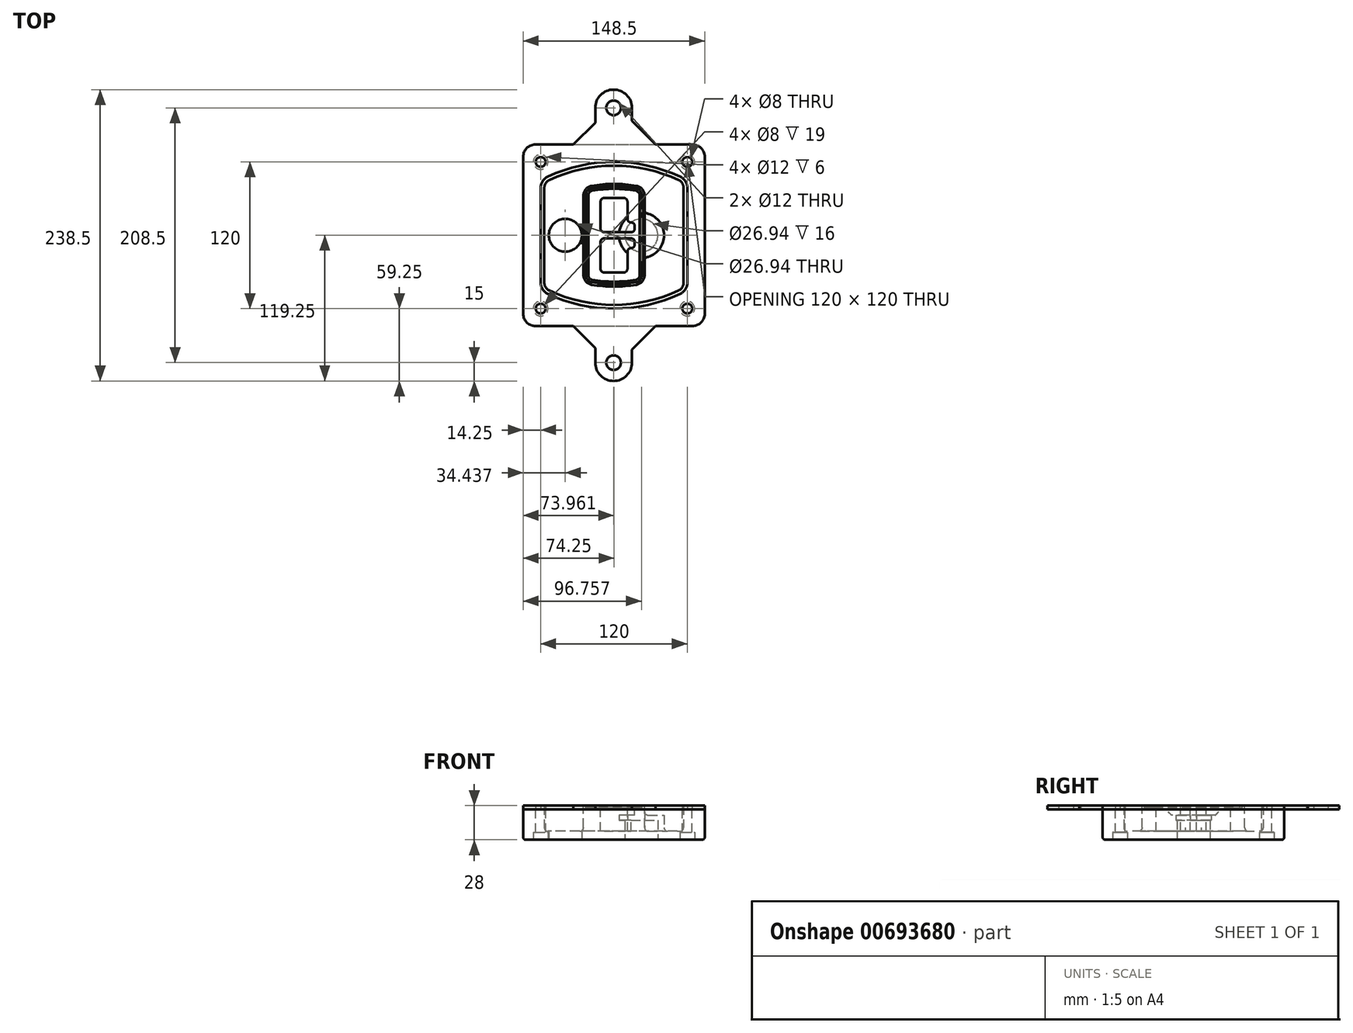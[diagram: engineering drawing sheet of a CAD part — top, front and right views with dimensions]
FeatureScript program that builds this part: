
annotation { "Feature Type Name" : "Feature", "Feature Type Description" : "" }
export const myFeature = defineFeature(function(context is Context, id is Id, definition is map)
    precondition{}
    {
        {
            var Q0;
            Q0=qCreatedBy(makeId("Top.planeOp"),FACE);
            var sketch = newSketch(context, id + "F0", { "sketchPlane" : qUnion([Q0])});
            skPoint(sketch, "E0.rect.middle", {"position": v(0, 0) * mm});
            skLineSegment(sketch, "E1.bottom", {"start": v(-64.25, -74.25) * mm, "end": v(64.25, -74.25) * mm});
            skLineSegment(sketch, "E1.top", {"start": v(-64.25, 74.25) * mm, "end": v(64.25, 74.25) * mm});
            skLineSegment(sketch, "E1.left", {"start": v(-74.25, -64.25) * mm, "end": v(-74.25, 64.25) * mm});
            skLineSegment(sketch, "E1.right", {"start": v(74.25, -64.25) * mm, "end": v(74.25, 64.25) * mm});
            skLineSegment(sketch, "E2", {"start": v(-74.25, 74.25) * mm, "end": v(74.25, -74.25) * mm, "construction": true});
            skLineSegment(sketch, "E3", {"start": v(74.25, 74.25) * mm, "end": v(-74.25, -74.25) * mm, "construction": true});
            skCircle(sketch, "E4", {"center": v(-60, 60) * mm, "radius": 4 * mm});
            skCircle(sketch, "E5", {"center": v(60, 60) * mm, "radius": 4 * mm});
            skCircle(sketch, "E6", {"center": v(60, -60) * mm, "radius": 4 * mm});
            skCircle(sketch, "E7", {"center": v(-60, -60) * mm, "radius": 4 * mm});
            skLineSegment(sketch, "E8", {"start": v(-60, 60) * mm, "end": v(60, 60) * mm, "construction": true});
            skLineSegment(sketch, "E9", {"start": v(60, 60) * mm, "end": v(60, -60) * mm, "construction": true});
            skLineSegment(sketch, "E10", {"start": v(60, -60) * mm, "end": v(-60, -60) * mm, "construction": true});
            skLineSegment(sketch, "E11", {"start": v(-60, -60) * mm, "end": v(-60, 60) * mm, "construction": true});
            skLineSegment(sketch, "E12", {"start": v(-60, 38.83) * mm, "end": v(-60, -38.83) * mm});
            skLineSegment(sketch, "E13", {"start": v(60, 38.83) * mm, "end": v(60, -38.83) * mm});
            skArc(sketch, "E14", {"start": v(54.26, 47.88) * mm, "mid": v(0, 60) * mm, "end": v(-54.26, 47.88) * mm});
            skArc(sketch, "E15", {"start": v(-54.26, -47.88) * mm, "mid": v(0, -60) * mm, "end": v(54.26, -47.88) * mm});
            skLineSegment(sketch, "E16", {"start": v(-60, 0) * mm, "end": v(60, 0) * mm, "construction": true});
            skPoint(sketch, "E17.visualSharp", {"position": v(-60, -45) * mm});
            skArc(sketch, "E17.filletArc", {"start": v(-60, -38.83) * mm, "mid": v(-58.44, -44.2) * mm, "end": v(-54.26, -47.88) * mm});
            skPoint(sketch, "E18.visualSharp", {"position": v(-60, 45) * mm});
            skArc(sketch, "E18.filletArc", {"start": v(-54.26, 47.88) * mm, "mid": v(-58.44, 44.2) * mm, "end": v(-60, 38.83) * mm});
            skPoint(sketch, "E19.visualSharp", {"position": v(60, 45) * mm});
            skArc(sketch, "E19.filletArc", {"start": v(60, 38.83) * mm, "mid": v(58.44, 44.2) * mm, "end": v(54.26, 47.88) * mm});
            skPoint(sketch, "E20.visualSharp", {"position": v(60, -45) * mm});
            skArc(sketch, "E20.filletArc", {"start": v(54.26, -47.88) * mm, "mid": v(58.44, -44.2) * mm, "end": v(60, -38.83) * mm});
            skPoint(sketch, "E21.visualSharp", {"position": v(-74.25, 74.25) * mm});
            skArc(sketch, "E21.filletArc", {"start": v(-64.25, 74.25) * mm, "mid": v(-71.32, 71.32) * mm, "end": v(-74.25, 64.25) * mm});
            skPoint(sketch, "E22.visualSharp", {"position": v(74.25, 74.25) * mm});
            skArc(sketch, "E22.filletArc", {"start": v(74.25, 64.25) * mm, "mid": v(71.32, 71.32) * mm, "end": v(64.25, 74.25) * mm});
            skPoint(sketch, "E23.visualSharp", {"position": v(74.25, -74.25) * mm});
            skArc(sketch, "E23.filletArc", {"start": v(64.25, -74.25) * mm, "mid": v(71.32, -71.32) * mm, "end": v(74.25, -64.25) * mm});
            skPoint(sketch, "E24.visualSharp", {"position": v(-74.25, -74.25) * mm});
            skArc(sketch, "E24.filletArc", {"start": v(-74.25, -64.25) * mm, "mid": v(-71.32, -71.32) * mm, "end": v(-64.25, -74.25) * mm});
            skArc(sketch, "E25.0", {"start": v(57, 38.83) * mm, "mid": v(55.9, 42.58) * mm, "end": v(52.98, 45.17) * mm});
            skLineSegment(sketch, "E25.1", {"start": v(57, 38.83) * mm, "end": v(57, -38.83) * mm});
            skArc(sketch, "E25.2", {"start": v(52.98, -45.17) * mm, "mid": v(55.9, -42.58) * mm, "end": v(57, -38.83) * mm});
            skArc(sketch, "E25.3", {"start": v(-52.98, -45.17) * mm, "mid": v(0, -57) * mm, "end": v(52.98, -45.17) * mm});
            skArc(sketch, "E25.4", {"start": v(-57, -38.83) * mm, "mid": v(-55.9, -42.58) * mm, "end": v(-52.98, -45.17) * mm});
            skArc(sketch, "E25.5", {"start": v(52.98, 45.17) * mm, "mid": v(0, 57) * mm, "end": v(-52.98, 45.17) * mm});
            skLineSegment(sketch, "E25.6", {"start": v(-57, 38.83) * mm, "end": v(-57, -38.83) * mm});
            skArc(sketch, "E25.7", {"start": v(-52.98, 45.17) * mm, "mid": v(-55.9, 42.58) * mm, "end": v(-57, 38.83) * mm});
            skArc(sketch, "E26.0", {"start": v(-55.96, 51.5) * mm, "mid": v(-61.82, 46.33) * mm, "end": v(-64, 38.83) * mm});
            skArc(sketch, "E26.1", {"start": v(55.96, 51.5) * mm, "mid": v(0, 64) * mm, "end": v(-55.96, 51.5) * mm});
            skArc(sketch, "E26.2", {"start": v(64, 38.83) * mm, "mid": v(61.82, 46.33) * mm, "end": v(55.96, 51.5) * mm});
            skLineSegment(sketch, "E26.3", {"start": v(64, 38.83) * mm, "end": v(64, -38.83) * mm});
            skArc(sketch, "E26.4", {"start": v(55.96, -51.5) * mm, "mid": v(61.82, -46.33) * mm, "end": v(64, -38.83) * mm});
            skLineSegment(sketch, "E26.5", {"start": v(-64, 38.83) * mm, "end": v(-64, -38.83) * mm});
            skArc(sketch, "E26.6", {"start": v(-55.96, -51.5) * mm, "mid": v(0, -64) * mm, "end": v(55.96, -51.5) * mm});
            skArc(sketch, "E26.7", {"start": v(-64, -38.83) * mm, "mid": v(-61.82, -46.33) * mm, "end": v(-55.96, -51.5) * mm});
            skSolve(sketch);
        }
        {
            var Q0;
            Q0=makeQuery(id+"F0.imprint","IMPRINT",FACE,{"disambiguationData":[TD([[makeQuery(id+"F0.imprint","IMPRINT",EDGE,{"derivedFrom":sQuery(id+"F0.wireOp",EDGE,"E1.bottom")}),1.0]])]});
            var Q1;
            Q1=makeQuery(id+"F0.imprint","IMPRINT",FACE,{"disambiguationData":[TD([[makeQuery(id+"F0.imprint","IMPRINT",EDGE,{"derivedFrom":sQuery(id+"F0.wireOp",EDGE,"E12")}),1.0]])]});
            var Q2;
            Q2=makeQuery(id+"F0.imprint","IMPRINT",FACE,{"disambiguationData":[TD([[makeQuery(id+"F0.imprint","IMPRINT",EDGE,{"derivedFrom":sQuery(id+"F0.wireOp",EDGE,"E25.0")}),1.0]])]});
            var Q3;
            Q3=makeQuery(id+"F0.imprint","IMPRINT",FACE,{"disambiguationData":[TD([[makeQuery(id+"F0.imprint","IMPRINT",EDGE,{"derivedFrom":sQuery(id+"F0.wireOp",EDGE,"E12")}),-1.0]])]});
            extrude(context, id + "F1", {"entities" : qUnion([Q0, Q1, Q2, Q3]), "oppositeDirection" : true, "depth" : 25 * mm});
        }
        {
            var Q0;
            Q0=makeQuery(id+"F0.imprint","IMPRINT",FACE,{"disambiguationData":[TD([[makeQuery(id+"F0.imprint","IMPRINT",EDGE,{"derivedFrom":sQuery(id+"F0.wireOp",EDGE,"E12")}),1.0]])]});
            extrude(context, id + "F2", {"entities" : qUnion([Q0]), "operationType" : NewBodyOperationType.ADD, "depth" : 3 * mm});
        }
        {
            var Q0;
            Q0=makeQuery(id+"F0.imprint","IMPRINT",FACE,{"disambiguationData":[TD([[makeQuery(id+"F0.imprint","IMPRINT",EDGE,{"derivedFrom":sQuery(id+"F0.wireOp",EDGE,"E25.0")}),1.0]])]});
            extrude(context, id + "F3", {"entities" : qUnion([Q0]), "operationType" : NewBodyOperationType.REMOVE, "oppositeDirection" : true, "depth" : 18 * mm});
        }
        {
            var Q0;
            Q0=makeQuery(id+"F2.opExtrude","CAP_FACE",FACE,{"disambiguationData":[OSD([sQuery(id+"F0.wireOp",EDGE,"E12"),sQuery(id+"F0.wireOp",EDGE,"E13"),sQuery(id+"F0.wireOp",EDGE,"E14"),sQuery(id+"F0.wireOp",EDGE,"E15"),sQuery(id+"F0.wireOp",EDGE,"E17.filletArc"),sQuery(id+"F0.wireOp",EDGE,"E18.filletArc"),sQuery(id+"F0.wireOp",EDGE,"E19.filletArc"),sQuery(id+"F0.wireOp",EDGE,"E20.filletArc"),sQuery(id+"F0.wireOp",EDGE,"E25.0"),sQuery(id+"F0.wireOp",EDGE,"E25.1"),sQuery(id+"F0.wireOp",EDGE,"E25.2"),sQuery(id+"F0.wireOp",EDGE,"E25.3"),sQuery(id+"F0.wireOp",EDGE,"E25.4"),sQuery(id+"F0.wireOp",EDGE,"E25.5"),sQuery(id+"F0.wireOp",EDGE,"E25.6"),sQuery(id+"F0.wireOp",EDGE,"E25.7")])],"isStart":false});
            var sketch = newSketch(context, id + "F4", { "sketchPlane" : qUnion([Q0])});
            skArc(sketch, "E27.0", {"start": v(-18.34, -40.45) * mm, "mid": v(0, -42) * mm, "end": v(18.34, -40.45) * mm});
            skArc(sketch, "E28.0", {"start": v(18.34, 40.45) * mm, "mid": v(0, 42) * mm, "end": v(-18.34, 40.45) * mm});
            skLineSegment(sketch, "E29", {"start": v(-25, 32.57) * mm, "end": v(-25, -32.57) * mm});
            skLineSegment(sketch, "E30", {"start": v(25, 32.57) * mm, "end": v(25, -32.57) * mm});
            skLineSegment(sketch, "E31", {"start": v(-25, 39.1) * mm, "end": v(25, 39.1) * mm, "construction": true});
            skLineSegment(sketch, "E32", {"start": v(-25, -39.1) * mm, "end": v(25, -39.1) * mm, "construction": true});
            skPoint(sketch, "E33.visualSharp", {"position": v(-25, 39.1) * mm});
            skArc(sketch, "E33.filletArc", {"start": v(-18.34, 40.45) * mm, "mid": v(-23.11, 37.73) * mm, "end": v(-25, 32.57) * mm});
            skPoint(sketch, "E34.visualSharp", {"position": v(25, 39.1) * mm});
            skArc(sketch, "E34.filletArc", {"start": v(25, 32.57) * mm, "mid": v(23.11, 37.73) * mm, "end": v(18.34, 40.45) * mm});
            skPoint(sketch, "E35.visualSharp", {"position": v(25, -39.1) * mm});
            skArc(sketch, "E35.filletArc", {"start": v(18.34, -40.45) * mm, "mid": v(23.11, -37.73) * mm, "end": v(25, -32.57) * mm});
            skPoint(sketch, "E36.visualSharp", {"position": v(-25, -39.1) * mm});
            skArc(sketch, "E36.filletArc", {"start": v(-25, -32.57) * mm, "mid": v(-23.11, -37.73) * mm, "end": v(-18.34, -40.45) * mm});
            skArc(sketch, "E37.0", {"start": v(52.98, 45.17) * mm, "mid": v(0, 57) * mm, "end": v(-52.98, 45.17) * mm});
            skArc(sketch, "E37.1", {"start": v(-52.98, 45.17) * mm, "mid": v(-55.9, 42.58) * mm, "end": v(-57, 38.83) * mm});
            skLineSegment(sketch, "E37.2", {"start": v(-57, 38.83) * mm, "end": v(-57, -38.83) * mm});
            skArc(sketch, "E37.3", {"start": v(-57, -38.83) * mm, "mid": v(-55.9, -42.58) * mm, "end": v(-52.98, -45.17) * mm});
            skArc(sketch, "E37.4", {"start": v(-52.98, -45.17) * mm, "mid": v(0, -57) * mm, "end": v(52.98, -45.17) * mm});
            skArc(sketch, "E37.5", {"start": v(52.98, -45.17) * mm, "mid": v(55.9, -42.58) * mm, "end": v(57, -38.83) * mm});
            skLineSegment(sketch, "E37.6", {"start": v(57, 38.83) * mm, "end": v(57, -38.83) * mm});
            skArc(sketch, "E37.7", {"start": v(57, 38.83) * mm, "mid": v(55.9, 42.58) * mm, "end": v(52.98, 45.17) * mm});
            skLineSegment(sketch, "E38.0", {"start": v(23, 32.57) * mm, "end": v(23, -32.57) * mm});
            skArc(sketch, "E38.1", {"start": v(18, -38.48) * mm, "mid": v(21.58, -36.44) * mm, "end": v(23, -32.57) * mm});
            skArc(sketch, "E38.2", {"start": v(-18, -38.48) * mm, "mid": v(0, -40) * mm, "end": v(18, -38.48) * mm});
            skArc(sketch, "E38.3", {"start": v(-23, -32.57) * mm, "mid": v(-21.58, -36.44) * mm, "end": v(-18, -38.48) * mm});
            skLineSegment(sketch, "E38.4", {"start": v(-23, 32.57) * mm, "end": v(-23, -32.57) * mm});
            skArc(sketch, "E38.5", {"start": v(23, 32.57) * mm, "mid": v(21.58, 36.44) * mm, "end": v(18, 38.48) * mm});
            skArc(sketch, "E38.6", {"start": v(-18, 38.48) * mm, "mid": v(-21.58, 36.44) * mm, "end": v(-23, 32.57) * mm});
            skArc(sketch, "E38.7", {"start": v(18, 38.48) * mm, "mid": v(0, 40) * mm, "end": v(-18, 38.48) * mm});
            skArc(sketch, "E39.0", {"start": v(21, 32.57) * mm, "mid": v(20.06, 35.15) * mm, "end": v(17.67, 36.5) * mm});
            skLineSegment(sketch, "E39.1", {"start": v(21, 32.57) * mm, "end": v(21, -32.57) * mm});
            skArc(sketch, "E39.2", {"start": v(17.67, -36.5) * mm, "mid": v(20.06, -35.15) * mm, "end": v(21, -32.57) * mm});
            skArc(sketch, "E39.3", {"start": v(-17.67, -36.5) * mm, "mid": v(0, -38) * mm, "end": v(17.67, -36.5) * mm});
            skArc(sketch, "E39.4", {"start": v(-21, -32.57) * mm, "mid": v(-20.06, -35.15) * mm, "end": v(-17.67, -36.5) * mm});
            skArc(sketch, "E39.5", {"start": v(17.67, 36.5) * mm, "mid": v(0, 38) * mm, "end": v(-17.67, 36.5) * mm});
            skLineSegment(sketch, "E39.6", {"start": v(-21, 32.57) * mm, "end": v(-21, -32.57) * mm});
            skArc(sketch, "E39.7", {"start": v(-17.67, 36.5) * mm, "mid": v(-20.06, 35.15) * mm, "end": v(-21, 32.57) * mm});
            skLineSegment(sketch, "E40", {"start": v(-25, 0) * mm, "end": v(25, 0) * mm, "construction": true});
            skLineSegment(sketch, "E41", {"start": v(-11, 5.5) * mm, "end": v(-11, 27.5) * mm});
            skLineSegment(sketch, "E42", {"start": v(-8, 30.5) * mm, "end": v(8, 30.5) * mm});
            skLineSegment(sketch, "E43", {"start": v(11, 27.5) * mm, "end": v(11, 13.5) * mm});
            skLineSegment(sketch, "E44", {"start": v(14, 10.5) * mm, "end": v(14, 10.5) * mm});
            skLineSegment(sketch, "E45", {"start": v(17, 7.5) * mm, "end": v(17, 5.5) * mm});
            skLineSegment(sketch, "E46", {"start": v(14, 2.5) * mm, "end": v(-8, 2.5) * mm});
            skPoint(sketch, "E47.visualSharp", {"position": v(-11, 30.5) * mm});
            skArc(sketch, "E47.filletArc", {"start": v(-8, 30.5) * mm, "mid": v(-10.12, 29.62) * mm, "end": v(-11, 27.5) * mm});
            skPoint(sketch, "E48.visualSharp", {"position": v(11, 30.5) * mm});
            skArc(sketch, "E48.filletArc", {"start": v(11, 27.5) * mm, "mid": v(10.12, 29.62) * mm, "end": v(8, 30.5) * mm});
            skPoint(sketch, "E49.visualSharp", {"position": v(11, 10.5) * mm});
            skArc(sketch, "E49.filletArc", {"start": v(11, 13.5) * mm, "mid": v(11.88, 11.38) * mm, "end": v(14, 10.5) * mm});
            skPoint(sketch, "E50.visualSharp", {"position": v(17, 10.5) * mm});
            skArc(sketch, "E50.filletArc", {"start": v(17, 7.5) * mm, "mid": v(16.12, 9.62) * mm, "end": v(14, 10.5) * mm});
            skPoint(sketch, "E51.visualSharp", {"position": v(17, 2.5) * mm});
            skArc(sketch, "E51.filletArc", {"start": v(14, 2.5) * mm, "mid": v(16.12, 3.38) * mm, "end": v(17, 5.5) * mm});
            skPoint(sketch, "E52.visualSharp", {"position": v(-11, 2.5) * mm});
            skArc(sketch, "E52.filletArc", {"start": v(-11, 5.5) * mm, "mid": v(-10.12, 3.38) * mm, "end": v(-8, 2.5) * mm});
            skLineSegment(sketch, "E53.0.MirrorCS", {"start": v(14, -2.5) * mm, "end": v(-8, -2.5) * mm});
            skArc(sketch, "E54.0.MirrorCS", {"start": v(-11, -5.5) * mm, "mid": v(-10.12, -3.38) * mm, "end": v(-8, -2.5) * mm});
            skLineSegment(sketch, "E55.0.MirrorCS", {"start": v(-11, -5.5) * mm, "end": v(-11, -27.5) * mm});
            skArc(sketch, "E56.0.MirrorCS", {"start": v(-8, -30.5) * mm, "mid": v(-10.12, -29.62) * mm, "end": v(-11, -27.5) * mm});
            skLineSegment(sketch, "E57.0.MirrorCS", {"start": v(-8, -30.5) * mm, "end": v(8, -30.5) * mm});
            skArc(sketch, "E58.0.MirrorCS", {"start": v(11, -27.5) * mm, "mid": v(10.12, -29.62) * mm, "end": v(8, -30.5) * mm});
            skLineSegment(sketch, "E59.0.MirrorCS", {"start": v(11, -27.5) * mm, "end": v(11, -13.5) * mm});
            skArc(sketch, "E60.0.MirrorCS", {"start": v(11, -13.5) * mm, "mid": v(11.88, -11.38) * mm, "end": v(14, -10.5) * mm});
            skArc(sketch, "E61.0.MirrorCS", {"start": v(17, -7.5) * mm, "mid": v(16.12, -9.62) * mm, "end": v(14, -10.5) * mm});
            skLineSegment(sketch, "E62.0.MirrorCS", {"start": v(17, -7.5) * mm, "end": v(17, -5.5) * mm});
            skArc(sketch, "E63.0.MirrorCS", {"start": v(14, -2.5) * mm, "mid": v(16.12, -3.38) * mm, "end": v(17, -5.5) * mm});
            skSolve(sketch);
        }
        {
            var Q0;
            Q0=makeQuery(id+"F4.imprint","IMPRINT",FACE,{"disambiguationData":[TD([[makeQuery(id+"F4.imprint","IMPRINT",EDGE,{"derivedFrom":sQuery(id+"F4.wireOp",EDGE,"E27.0")}),1.0]])]});
            var Q1;
            Q1=makeQuery(id+"F4.imprint","IMPRINT",FACE,{"disambiguationData":[TD([[makeQuery(id+"F4.imprint","IMPRINT",EDGE,{"derivedFrom":sQuery(id+"F4.wireOp",EDGE,"E38.0")}),-1.0]])]});
            var Q2;
            Q2=makeQuery(id+"F4.imprint","IMPRINT",FACE,{"disambiguationData":[TD([[makeQuery(id+"F4.imprint","IMPRINT",EDGE,{"derivedFrom":sQuery(id+"F4.wireOp",EDGE,"E39.0")}),1.0]])]});
            extrude(context, id + "F5", {"entities" : qUnion([Q0, Q1, Q2]), "operationType" : NewBodyOperationType.ADD, "endBound" : BoundingType.UP_TO_NEXT, "oppositeDirection" : true, "depth" : 25 * mm});
        }
        {
            var Q0;
            Q0=makeQuery(id+"F4.imprint","IMPRINT",FACE,{"disambiguationData":[TD([[makeQuery(id+"F4.imprint","IMPRINT",EDGE,{"derivedFrom":sQuery(id+"F4.wireOp",EDGE,"E38.0")}),-1.0]])]});
            extrude(context, id + "F6", {"entities" : qUnion([Q0]), "operationType" : NewBodyOperationType.REMOVE, "oppositeDirection" : true, "depth" : 2 * mm});
        }
        {
            var Q0;
            Q0=makeQuery(id+"F1.opExtrude","CAP_FACE",FACE,{"disambiguationData":[OSD([sQuery(id+"F0.wireOp",EDGE,"E1.bottom"),sQuery(id+"F0.wireOp",EDGE,"E1.top"),sQuery(id+"F0.wireOp",EDGE,"E1.left"),sQuery(id+"F0.wireOp",EDGE,"E1.right"),sQuery(id+"F0.wireOp",EDGE,"E4"),sQuery(id+"F0.wireOp",EDGE,"E5"),sQuery(id+"F0.wireOp",EDGE,"E6"),sQuery(id+"F0.wireOp",EDGE,"E7"),sQuery(id+"F0.wireOp",EDGE,"E21.filletArc"),sQuery(id+"F0.wireOp",EDGE,"E22.filletArc"),sQuery(id+"F0.wireOp",EDGE,"E23.filletArc"),sQuery(id+"F0.wireOp",EDGE,"E24.filletArc")])],"isStart":false});
            var sketch = newSketch(context, id + "F7", { "sketchPlane" : qUnion([Q0])});
            skCircle(sketch, "E64", {"center": v(22.5, 0) * mm, "radius": 13.47 * mm});
            skCircle(sketch, "E65", {"center": v(-39.81, 0) * mm, "radius": 13.47 * mm});
            skLineSegment(sketch, "E66", {"start": v(74.25, 0) * mm, "end": v(-74.25, 0) * mm});
            skCircle(sketch, "E67", {"center": v(22.5, 0) * mm, "radius": 18.47 * mm});
            skCircle(sketch, "E68", {"center": v(60, -60) * mm, "radius": 6 * mm});
            skCircle(sketch, "E69", {"center": v(-60, -60) * mm, "radius": 6 * mm});
            skCircle(sketch, "E70", {"center": v(-60, 60) * mm, "radius": 6 * mm});
            skCircle(sketch, "E71", {"center": v(60, 60) * mm, "radius": 6 * mm});
            skSolve(sketch);
        }
        {
            var Q0;
            {var subQ1=sQuery(id+"F7.wireOp",EDGE,"E66");var subQ4=sQuery(id+"F7.wireOp",EDGE,"E64");var subQ6=makeQuery(id+"F7.imprint","INTERSECT",VERTEX,{"disambiguationData":[OD(0.0)],"derivedFrom":[subQ4,subQ1]});Q0=makeQuery(id+"F7.imprint","IMPRINT",FACE,{"disambiguationData":[TD([[makeQuery(id+"F7.imprint","IMPRINT",EDGE,{"disambiguationData":[TD([[subQ6,-1.0]])],"derivedFrom":subQ4}),-1.0]])]});}
            var Q1;
            {var subQ0=sQuery(id+"F7.wireOp",EDGE,"E66");var subQ1=sQuery(id+"F7.wireOp",EDGE,"E64");var subQ3=makeQuery(id+"F7.imprint","INTERSECT",VERTEX,{"disambiguationData":[OD(0.0)],"derivedFrom":[subQ1,subQ0]});Q1=makeQuery(id+"F7.imprint","IMPRINT",FACE,{"disambiguationData":[TD([[makeQuery(id+"F7.imprint","IMPRINT",EDGE,{"disambiguationData":[TD([[subQ3,-1.0]])],"derivedFrom":subQ1}),1.0]])]});}
            var Q2;
            {var subQ0=sQuery(id+"F7.wireOp",EDGE,"E66");var subQ1=sQuery(id+"F7.wireOp",EDGE,"E64");var subQ3=makeQuery(id+"F7.imprint","INTERSECT",VERTEX,{"disambiguationData":[OD(0.0)],"derivedFrom":[subQ1,subQ0]});Q2=makeQuery(id+"F7.imprint","IMPRINT",FACE,{"disambiguationData":[TD([[makeQuery(id+"F7.imprint","IMPRINT",EDGE,{"disambiguationData":[TD([[subQ3,1.0]])],"derivedFrom":subQ1}),1.0]])]});}
            var Q3;
            {var subQ1=sQuery(id+"F7.wireOp",EDGE,"E66");var subQ4=sQuery(id+"F7.wireOp",EDGE,"E64");var subQ6=makeQuery(id+"F7.imprint","INTERSECT",VERTEX,{"disambiguationData":[OD(0.0)],"derivedFrom":[subQ4,subQ1]});Q3=makeQuery(id+"F7.imprint","IMPRINT",FACE,{"disambiguationData":[TD([[makeQuery(id+"F7.imprint","IMPRINT",EDGE,{"disambiguationData":[TD([[subQ6,1.0]])],"derivedFrom":subQ4}),-1.0]])]});}
            extrude(context, id + "F8", {"entities" : qUnion([Q0, Q1, Q2, Q3]), "operationType" : NewBodyOperationType.ADD, "oppositeDirection" : true, "depth" : 20 * mm});
        }
        {
            var Q0;
            {var subQ0=sQuery(id+"F7.wireOp",EDGE,"E66");var subQ1=sQuery(id+"F7.wireOp",EDGE,"E64");var subQ3=makeQuery(id+"F7.imprint","INTERSECT",VERTEX,{"disambiguationData":[OD(0.0)],"derivedFrom":[subQ1,subQ0]});Q0=makeQuery(id+"F7.imprint","IMPRINT",FACE,{"disambiguationData":[TD([[makeQuery(id+"F7.imprint","IMPRINT",EDGE,{"disambiguationData":[TD([[subQ3,-1.0]])],"derivedFrom":subQ1}),1.0]])]});}
            var Q1;
            {var subQ0=sQuery(id+"F7.wireOp",EDGE,"E66");var subQ1=sQuery(id+"F7.wireOp",EDGE,"E64");var subQ3=makeQuery(id+"F7.imprint","INTERSECT",VERTEX,{"disambiguationData":[OD(0.0)],"derivedFrom":[subQ1,subQ0]});Q1=makeQuery(id+"F7.imprint","IMPRINT",FACE,{"disambiguationData":[TD([[makeQuery(id+"F7.imprint","IMPRINT",EDGE,{"disambiguationData":[TD([[subQ3,1.0]])],"derivedFrom":subQ1}),1.0]])]});}
            extrude(context, id + "F9", {"entities" : qUnion([Q0, Q1]), "operationType" : NewBodyOperationType.REMOVE, "oppositeDirection" : true, "depth" : 16 * mm});
        }
        {
            var Q0;
            {var subQ0=sQuery(id+"F7.wireOp",EDGE,"E66");var subQ1=sQuery(id+"F7.wireOp",EDGE,"E65");var subQ3=makeQuery(id+"F7.imprint","INTERSECT",VERTEX,{"disambiguationData":[OD(0.0)],"derivedFrom":[subQ1,subQ0]});Q0=makeQuery(id+"F7.imprint","IMPRINT",FACE,{"disambiguationData":[TD([[makeQuery(id+"F7.imprint","IMPRINT",EDGE,{"disambiguationData":[TD([[subQ3,-1.0]])],"derivedFrom":subQ1}),1.0]])]});}
            var Q1;
            {var subQ0=sQuery(id+"F7.wireOp",EDGE,"E66");var subQ1=sQuery(id+"F7.wireOp",EDGE,"E65");var subQ3=makeQuery(id+"F7.imprint","INTERSECT",VERTEX,{"disambiguationData":[OD(0.0)],"derivedFrom":[subQ1,subQ0]});Q1=makeQuery(id+"F7.imprint","IMPRINT",FACE,{"disambiguationData":[TD([[makeQuery(id+"F7.imprint","IMPRINT",EDGE,{"disambiguationData":[TD([[subQ3,1.0]])],"derivedFrom":subQ1}),1.0]])]});}
            extrude(context, id + "F10", {"entities" : qUnion([Q0, Q1]), "operationType" : NewBodyOperationType.REMOVE, "oppositeDirection" : true, "depth" : 25 * mm});
        }
        {
            var Q0;
            Q0=makeQuery(id+"F7.imprint","IMPRINT",FACE,{"disambiguationData":[TD([[makeQuery(id+"F7.imprint","IMPRINT",EDGE,{"derivedFrom":sQuery(id+"F7.wireOp",EDGE,"E68")}),1.0]])]});
            var Q1;
            Q1=makeQuery(id+"F7.imprint","IMPRINT",FACE,{"disambiguationData":[TD([[makeQuery(id+"F7.imprint","IMPRINT",EDGE,{"derivedFrom":makeQuery(id+"F1.opExtrude","CAP_EDGE",EDGE,{"disambiguationData":[OSD([sQuery(id+"F0.wireOp",EDGE,"E5")])],"isStart":false})}),-1.0]])]});
            var Q2;
            Q2=makeQuery(id+"F7.imprint","IMPRINT",FACE,{"disambiguationData":[TD([[makeQuery(id+"F7.imprint","IMPRINT",EDGE,{"derivedFrom":sQuery(id+"F7.wireOp",EDGE,"E69")}),1.0]])]});
            var Q3;
            Q3=makeQuery(id+"F7.imprint","IMPRINT",FACE,{"disambiguationData":[TD([[makeQuery(id+"F7.imprint","IMPRINT",EDGE,{"derivedFrom":makeQuery(id+"F1.opExtrude","CAP_EDGE",EDGE,{"disambiguationData":[OSD([sQuery(id+"F0.wireOp",EDGE,"E4")])],"isStart":false})}),-1.0]])]});
            var Q4;
            Q4=makeQuery(id+"F7.imprint","IMPRINT",FACE,{"disambiguationData":[TD([[makeQuery(id+"F7.imprint","IMPRINT",EDGE,{"derivedFrom":sQuery(id+"F7.wireOp",EDGE,"E70")}),1.0]])]});
            var Q5;
            Q5=makeQuery(id+"F7.imprint","IMPRINT",FACE,{"disambiguationData":[TD([[makeQuery(id+"F7.imprint","IMPRINT",EDGE,{"derivedFrom":makeQuery(id+"F1.opExtrude","CAP_EDGE",EDGE,{"disambiguationData":[OSD([sQuery(id+"F0.wireOp",EDGE,"E7")])],"isStart":false})}),-1.0]])]});
            var Q6;
            Q6=makeQuery(id+"F7.imprint","IMPRINT",FACE,{"disambiguationData":[TD([[makeQuery(id+"F7.imprint","IMPRINT",EDGE,{"derivedFrom":sQuery(id+"F7.wireOp",EDGE,"E71")}),1.0]])]});
            var Q7;
            Q7=makeQuery(id+"F7.imprint","IMPRINT",FACE,{"disambiguationData":[TD([[makeQuery(id+"F7.imprint","IMPRINT",EDGE,{"derivedFrom":makeQuery(id+"F1.opExtrude","CAP_EDGE",EDGE,{"disambiguationData":[OSD([sQuery(id+"F0.wireOp",EDGE,"E6")])],"isStart":false})}),-1.0]])]});
            extrude(context, id + "F11", {"entities" : qUnion([Q0, Q1, Q2, Q3, Q4, Q5, Q6, Q7]), "operationType" : NewBodyOperationType.REMOVE, "oppositeDirection" : true, "depth" : 6 * mm});
        }
        {
            var Q0;
            Q0=makeQuery(id+"F9.boolean.opBoolean","COPY",FACE,{"derivedFrom":makeQuery(id+"F9.opExtrude","CAP_FACE",FACE,{"disambiguationData":[OSD([sQuery(id+"F7.wireOp",EDGE,"E64")])],"isStart":false})});
            var sketch = newSketch(context, id + "F12", { "sketchPlane" : qUnion([Q0])});
            skArc(sketch, "E72.0", {"start": v(11, 14.45) * mm, "mid": v(6.45, 9.13) * mm, "end": v(4.2, 2.5) * mm});
            skArc(sketch, "E72.1", {"start": v(4.2, -2.5) * mm, "mid": v(6.45, -9.13) * mm, "end": v(11, -14.45) * mm});
            skLineSegment(sketch, "E73", {"start": v(4.2, -2.5) * mm, "end": v(14, -2.5) * mm});
            skLineSegment(sketch, "E74.0", {"start": v(14, 2.5) * mm, "end": v(4.2, 2.5) * mm});
            skArc(sketch, "E74.1", {"start": v(14, 2.5) * mm, "mid": v(16.12, 3.38) * mm, "end": v(17, 5.5) * mm});
            skLineSegment(sketch, "E74.2", {"start": v(17, 7.5) * mm, "end": v(17, 5.5) * mm});
            skArc(sketch, "E74.3", {"start": v(17, 7.5) * mm, "mid": v(16.12, 9.62) * mm, "end": v(14, 10.5) * mm});
            skArc(sketch, "E74.4", {"start": v(11, 13.5) * mm, "mid": v(11.88, 11.38) * mm, "end": v(14, 10.5) * mm});
            skLineSegment(sketch, "E74.5", {"start": v(11, 14.45) * mm, "end": v(11, 13.5) * mm});
            skLineSegment(sketch, "E74.7", {"start": v(14, -2.5) * mm, "end": v(4.2, -2.5) * mm});
            skArc(sketch, "E74.8", {"start": v(14, -2.5) * mm, "mid": v(16.12, -3.38) * mm, "end": v(17, -5.5) * mm});
            skLineSegment(sketch, "E74.9", {"start": v(17, -7.5) * mm, "end": v(17, -5.5) * mm});
            skArc(sketch, "E74.10", {"start": v(17, -7.5) * mm, "mid": v(16.12, -9.62) * mm, "end": v(14, -10.5) * mm});
            skArc(sketch, "E74.11", {"start": v(11, -13.5) * mm, "mid": v(11.88, -11.38) * mm, "end": v(14, -10.5) * mm});
            skLineSegment(sketch, "E74.12", {"start": v(11, -14.45) * mm, "end": v(11, -13.5) * mm});
            skPoint(sketch, "E75.orphan", {"position": v(11, -27.5) * mm});
            skPoint(sketch, "E76.orphan", {"position": v(-8, -2.5) * mm});
            skPoint(sketch, "E77.orphan", {"position": v(-8, 2.5) * mm});
            skPoint(sketch, "E78.orphan", {"position": v(11, 27.5) * mm});
            skSolve(sketch);
        }
        {
            var Q0;
            {var subQ7=sQuery(id+"F12.wireOp",EDGE,"E72.0");var subQ14=sQuery(id+"F12.wireOp",EDGE,"E72.1");var subQ16=sQuery(id+"F12.wireOp",EDGE,"E74.1");var subQ18=sQuery(id+"F12.wireOp",EDGE,"E74.8");Q0=qUnion([makeQuery(id+"F12.imprint","IMPRINT",FACE,{"disambiguationData":[TD([[makeQuery(id+"F12.imprint","IMPRINT",EDGE,{"derivedFrom":subQ7}),1.0]])]}),makeQuery(id+"F12.imprint","IMPRINT",FACE,{"disambiguationData":[TD([[makeQuery(id+"F12.imprint","IMPRINT",EDGE,{"derivedFrom":subQ14}),1.0]])]}),makeQuery(id+"F12.imprint","IMPRINT",FACE,{"disambiguationData":[TD([[makeQuery(id+"F12.imprint","IMPRINT",EDGE,{"derivedFrom":subQ16}),1.0]])]}),makeQuery(id+"F12.imprint","IMPRINT",FACE,{"disambiguationData":[TD([[makeQuery(id+"F12.imprint","IMPRINT",EDGE,{"derivedFrom":subQ18}),-1.0]])]})]);}
            var Q1;
            Q1=makeQuery(id+"F5.boolean.opBoolean","SPLIT",FACE,{"disambiguationData":[TD([makeQuery(id+"F5.opExtrude","SWEPT_FACE",FACE,{"disambiguationData":[OSD([sQuery(id+"F4.wireOp",EDGE,"E41")])]})])],"derivedFrom":makeQuery(id+"F3.boolean.opBoolean","COPY",FACE,{"derivedFrom":makeQuery(id+"F3.opExtrude","CAP_FACE",FACE,{"disambiguationData":[OSD([sQuery(id+"F0.wireOp",EDGE,"E25.0"),sQuery(id+"F0.wireOp",EDGE,"E25.1"),sQuery(id+"F0.wireOp",EDGE,"E25.2"),sQuery(id+"F0.wireOp",EDGE,"E25.3"),sQuery(id+"F0.wireOp",EDGE,"E25.4"),sQuery(id+"F0.wireOp",EDGE,"E25.5"),sQuery(id+"F0.wireOp",EDGE,"E25.6"),sQuery(id+"F0.wireOp",EDGE,"E25.7")])],"isStart":false})})});
            extrude(context, id + "F13", {"entities" : qUnion([Q0]), "operationType" : NewBodyOperationType.REMOVE, "endBound" : BoundingType.UP_TO_SURFACE, "endBoundEntityFace" : qUnion([Q1]), "depth" : 25 * mm});
        }
        {
            var Q0;
            Q0=makeQuery(id+"F3.boolean.opBoolean","COPY",EDGE,{"derivedFrom":makeQuery(id+"F3.opExtrude","CAP_EDGE",EDGE,{"disambiguationData":[OSD([sQuery(id+"F0.wireOp",EDGE,"E25.6")])],"isStart":false})});
            var Q1;
            Q1=makeQuery(id+"F8.boolean.opBoolean","INTERSECT",EDGE,{"derivedFrom":[makeQuery(id+"F5.opExtrude","SWEPT_FACE",FACE,{"disambiguationData":[OSD([sQuery(id+"F4.wireOp",EDGE,"E30")])]}),makeQuery(id+"F8.opExtrude","CAP_FACE",FACE,{"disambiguationData":[OSD([sQuery(id+"F7.wireOp",EDGE,"E67")])],"isStart":false})]});
            var Q2;
            Q2=makeQuery(id+"F8.boolean.opBoolean","INTERSECT",EDGE,{"disambiguationData":[OD(1.0)],"derivedFrom":[makeQuery(id+"F5.opExtrude","SWEPT_FACE",FACE,{"disambiguationData":[OSD([sQuery(id+"F4.wireOp",EDGE,"E30")])]}),makeQuery(id+"F8.opExtrude","SWEPT_FACE",FACE,{"disambiguationData":[OSD([sQuery(id+"F7.wireOp",EDGE,"E67")])]})]});
            var Q3;
            {var subQ0=sQuery(id+"F4.wireOp",EDGE,"E30");Q3=makeQuery(id+"F8.boolean.opBoolean","SPLIT",EDGE,{"disambiguationData":[TD([makeQuery(id+"F5.opExtrude","SWEPT_FACE",FACE,{"disambiguationData":[OSD([sQuery(id+"F4.wireOp",EDGE,"E35.filletArc")])]})])],"derivedFrom":makeQuery(id+"F5.opExtrude","CAP_EDGE",EDGE,{"disambiguationData":[OSD([subQ0])],"isStart":false})});}
            var Q4;
            {var subQ0=sQuery(id+"F0.wireOp",EDGE,"E25.7");var subQ1=sQuery(id+"F0.wireOp",EDGE,"E25.1");var subQ2=sQuery(id+"F0.wireOp",EDGE,"E25.6");var subQ3=sQuery(id+"F0.wireOp",EDGE,"E25.5");var subQ4=sQuery(id+"F0.wireOp",EDGE,"E25.4");var subQ5=sQuery(id+"F0.wireOp",EDGE,"E25.0");var subQ6=sQuery(id+"F0.wireOp",EDGE,"E25.2");var subQ7=sQuery(id+"F0.wireOp",EDGE,"E25.3");Q4=makeQuery(id+"F8.boolean.opBoolean","INTERSECT",EDGE,{"derivedFrom":[makeQuery(id+"F5.boolean.opBoolean","SPLIT",FACE,{"disambiguationData":[TD([makeQuery(id+"F2.opExtrude","SWEPT_FACE",FACE,{"disambiguationData":[OSD([subQ5])]})])],"derivedFrom":makeQuery(id+"F3.boolean.opBoolean","COPY",FACE,{"derivedFrom":makeQuery(id+"F3.opExtrude","CAP_FACE",FACE,{"disambiguationData":[OSD([subQ5,subQ1,subQ6,subQ7,subQ4,subQ3,subQ2,subQ0])],"isStart":false})})}),makeQuery(id+"F8.opExtrude","SWEPT_FACE",FACE,{"disambiguationData":[OSD([sQuery(id+"F7.wireOp",EDGE,"E67")])]})]});}
            var Q5;
            Q5=makeQuery(id+"F8.boolean.opBoolean","INTERSECT",EDGE,{"disambiguationData":[OD(0.0)],"derivedFrom":[makeQuery(id+"F5.opExtrude","SWEPT_FACE",FACE,{"disambiguationData":[OSD([sQuery(id+"F4.wireOp",EDGE,"E30")])]}),makeQuery(id+"F8.opExtrude","SWEPT_FACE",FACE,{"disambiguationData":[OSD([sQuery(id+"F7.wireOp",EDGE,"E67")])]})]});
            fillet(context, id + "F14", {"entities" : qUnion([Q0, Q1, Q2, Q3, Q4, Q5]), "radius" : 3 * mm, "tangentPropagation" : true, "allowEdgeOverflow" : false});
        }
        {
            var Q0;
            Q0=makeQuery(id+"F1.opExtrude","CAP_EDGE",EDGE,{"disambiguationData":[OSD([sQuery(id+"F0.wireOp",EDGE,"E1.bottom")])],"isStart":false});
            fillet(context, id + "F15", {"entities" : qUnion([Q0]), "radius" : 2 * mm, "tangentPropagation" : true, "allowEdgeOverflow" : false});
        }
        {
            var Q0;
            {var subQ0=sQuery(id+"F0.wireOp",EDGE,"E21.filletArc");var subQ1=sQuery(id+"F0.wireOp",EDGE,"E7");var subQ2=sQuery(id+"F0.wireOp",EDGE,"E6");var subQ3=sQuery(id+"F0.wireOp",EDGE,"E5");var subQ4=sQuery(id+"F0.wireOp",EDGE,"E4");var subQ5=sQuery(id+"F0.wireOp",EDGE,"E22.filletArc");var subQ6=sQuery(id+"F0.wireOp",EDGE,"E1.bottom");var subQ7=sQuery(id+"F0.wireOp",EDGE,"E1.right");var subQ8=sQuery(id+"F0.wireOp",EDGE,"E1.top");var subQ9=sQuery(id+"F0.wireOp",EDGE,"E1.left");var subQ10=sQuery(id+"F0.wireOp",EDGE,"E23.filletArc");var subQ11=sQuery(id+"F0.wireOp",EDGE,"E24.filletArc");Q0=makeQuery(id+"F2.boolean.opBoolean","SPLIT",FACE,{"disambiguationData":[TD([makeQuery(id+"F1.opExtrude","SWEPT_FACE",FACE,{"disambiguationData":[OSD([subQ6])]})])],"derivedFrom":makeQuery(id+"F1.opExtrude","CAP_FACE",FACE,{"disambiguationData":[OSD([subQ6,subQ8,subQ9,subQ7,subQ4,subQ3,subQ2,subQ1,subQ0,subQ5,subQ10,subQ11])],"isStart":true})});}
            var sketch = newSketch(context, id + "F16", { "sketchPlane" : qUnion([Q0])});
            skLineSegment(sketch, "E79", {"start": v(-0.29, 74.25) * mm, "end": v(-0.29, 104.25) * mm, "construction": true});
            skCircle(sketch, "E80", {"center": v(-0.29, 104.25) * mm, "radius": 6 * mm});
            skArc(sketch, "E81", {"start": v(-0.29, 119.25) * mm, "mid": v(10.32, 114.86) * mm, "end": v(14.71, 104.25) * mm});
            skArc(sketch, "E82", {"start": v(-0.29, 119.25) * mm, "mid": v(-10.9, 114.86) * mm, "end": v(-15.29, 104.25) * mm});
            skLineSegment(sketch, "E83", {"start": v(-15.29, 104.25) * mm, "end": v(-15.29, 92.25) * mm});
            skLineSegment(sketch, "E84", {"start": v(14.71, 104.25) * mm, "end": v(14.71, 93.54) * mm});
            skLineSegment(sketch, "E85", {"start": v(14.71, 93.54) * mm, "end": v(34, 74.25) * mm});
            skLineSegment(sketch, "E86", {"start": v(-15.29, 92.25) * mm, "end": v(-33.29, 74.25) * mm});
            skLineSegment(sketch, "E87", {"start": v(-74.25, 0) * mm, "end": v(74.25, 0) * mm, "construction": true});
            skLineSegment(sketch, "E88.MirrorCS", {"start": v(14.71, -93.54) * mm, "end": v(34, -74.25) * mm});
            skLineSegment(sketch, "E89.MirrorCS", {"start": v(14.71, -104.25) * mm, "end": v(14.71, -93.54) * mm});
            skArc(sketch, "E90.MirrorCS", {"start": v(-0.29, -119.25) * mm, "mid": v(10.32, -114.86) * mm, "end": v(14.71, -104.25) * mm});
            skArc(sketch, "E91.MirrorCS", {"start": v(-0.29, -119.25) * mm, "mid": v(-10.9, -114.86) * mm, "end": v(-15.29, -104.25) * mm});
            skLineSegment(sketch, "E92.MirrorCS", {"start": v(-15.29, -104.25) * mm, "end": v(-15.29, -92.25) * mm});
            skLineSegment(sketch, "E93.MirrorCS", {"start": v(-15.29, -92.25) * mm, "end": v(-33.29, -74.25) * mm});
            skLineSegment(sketch, "E94.MirrorCS", {"start": v(-0.29, -74.25) * mm, "end": v(-0.29, -104.25) * mm, "construction": true});
            skCircle(sketch, "E95.MirrorC", {"center": v(-0.29, -104.25) * mm, "radius": 6 * mm});
            skSolve(sketch);
        }
        {
            var Q0;
            Q0=makeQuery(id+"F16.imprint","IMPRINT",FACE,{"disambiguationData":[TD([[makeQuery(id+"F16.imprint","IMPRINT",EDGE,{"derivedFrom":sQuery(id+"F16.wireOp",EDGE,"E80")}),-1.0]])]});
            var Q1;
            Q1=makeQuery(id+"F16.imprint","IMPRINT",FACE,{"disambiguationData":[TD([[makeQuery(id+"F16.imprint","IMPRINT",EDGE,{"derivedFrom":makeQuery(id+"F1.opExtrude","CAP_EDGE",EDGE,{"disambiguationData":[OSD([sQuery(id+"F0.wireOp",EDGE,"E1.left")])],"isStart":true})}),-1.0]])]});
            var Q2;
            {var subQ0=sQuery(id+"F16.wireOp",EDGE,"E88.MirrorCS");Q2=makeQuery(id+"F16.imprint","IMPRINT",FACE,{"disambiguationData":[TD([[makeQuery(id+"F16.imprint","IMPRINT",EDGE,{"derivedFrom":subQ0}),1.0]])]});}
            var Q3;
            Q3=makeQuery(id+"F2.opExtrude","CAP_FACE",FACE,{"disambiguationData":[OSD([sQuery(id+"F0.wireOp",EDGE,"E12"),sQuery(id+"F0.wireOp",EDGE,"E13"),sQuery(id+"F0.wireOp",EDGE,"E14"),sQuery(id+"F0.wireOp",EDGE,"E15"),sQuery(id+"F0.wireOp",EDGE,"E17.filletArc"),sQuery(id+"F0.wireOp",EDGE,"E18.filletArc"),sQuery(id+"F0.wireOp",EDGE,"E19.filletArc"),sQuery(id+"F0.wireOp",EDGE,"E20.filletArc"),sQuery(id+"F0.wireOp",EDGE,"E25.0"),sQuery(id+"F0.wireOp",EDGE,"E25.1"),sQuery(id+"F0.wireOp",EDGE,"E25.2"),sQuery(id+"F0.wireOp",EDGE,"E25.3"),sQuery(id+"F0.wireOp",EDGE,"E25.4"),sQuery(id+"F0.wireOp",EDGE,"E25.5"),sQuery(id+"F0.wireOp",EDGE,"E25.6"),sQuery(id+"F0.wireOp",EDGE,"E25.7")])],"isStart":false});
            extrude(context, id + "F17", {"entities" : qUnion([Q0, Q1, Q2]), "endBound" : BoundingType.UP_TO_SURFACE, "depth" : 25 * mm, "endBoundEntityFace" : qUnion([Q3]), "offsetDistance" : 25 * mm});
        }
    });
